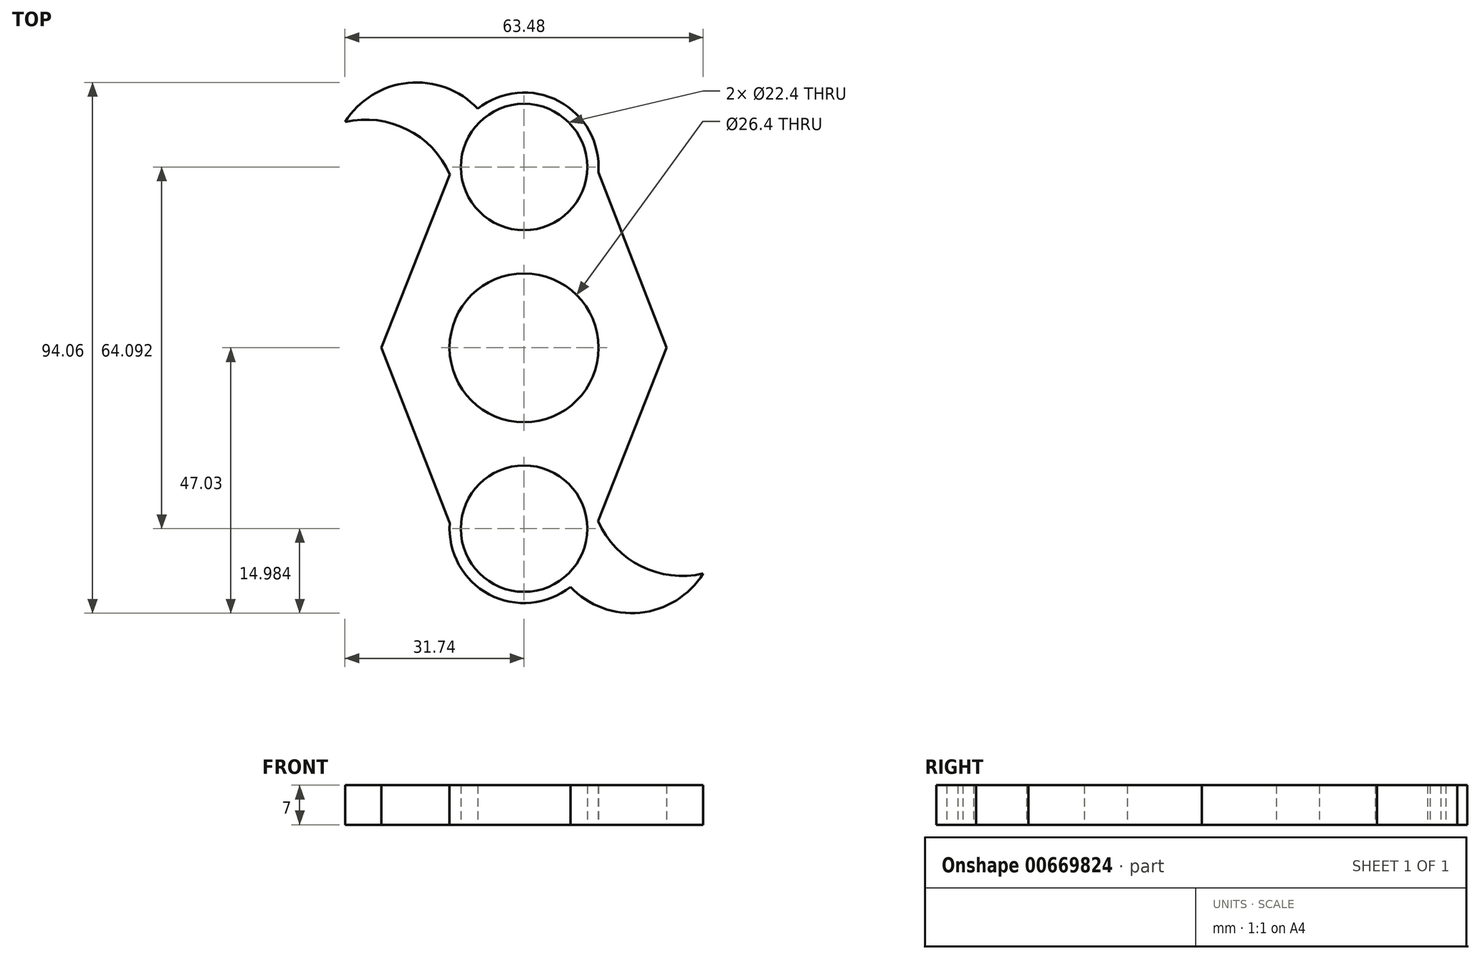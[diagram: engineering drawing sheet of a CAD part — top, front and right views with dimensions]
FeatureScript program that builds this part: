
annotation { "Feature Type Name" : "Feature", "Feature Type Description" : "" }
export const myFeature = defineFeature(function(context is Context, id is Id, definition is map)
    precondition{}
    {
        {
            var Q0;
            Q0=qCreatedBy(makeId("Top.planeOp"),FACE);
            var sketch = newSketch(context, id + "F0", { "sketchPlane" : qUnion([Q0])});
            skCircle(sketch, "E0", {"center": v(0, 0) * mm, "radius": 11.2 * mm});
            skCircle(sketch, "E1", {"center": v(0, 0) * mm, "radius": 13.2 * mm});
            skCircle(sketch, "E2", {"center": v(0, 32.05) * mm, "radius": 11.2 * mm});
            skCircle(sketch, "E3", {"center": v(0, 32.05) * mm, "radius": 13.2 * mm});
            skCircle(sketch, "E4.1.0", {"center": v(0, -32.05) * mm, "radius": 13.2 * mm});
            skCircle(sketch, "E4.1.1", {"center": v(0, -32.05) * mm, "radius": 11.2 * mm});
            skLineSegment(sketch, "E5", {"start": v(-13.13, 30.73) * mm, "end": v(-25.26, 0) * mm});
            skLineSegment(sketch, "E6", {"start": v(-25.26, 0) * mm, "end": v(-13.16, -31.07) * mm});
            skLineSegment(sketch, "E7.1.0", {"start": v(13.13, -30.73) * mm, "end": v(25.26, 0) * mm});
            skLineSegment(sketch, "E7.1.1", {"start": v(25.26, 0) * mm, "end": v(13.16, 31.07) * mm});
            skArc(sketch, "E8", {"start": v(-13.13, 30.73) * mm, "mid": v(-20.76, 38.72) * mm, "end": v(-31.74, 40) * mm});
            skArc(sketch, "E9", {"start": v(-8.22, 42.38) * mm, "mid": v(-20.56, 46.95) * mm, "end": v(-31.74, 40) * mm});
            skArc(sketch, "E10.1.0", {"start": v(8.22, -42.38) * mm, "mid": v(20.56, -46.95) * mm, "end": v(31.74, -40) * mm});
            skArc(sketch, "E10.1.1", {"start": v(13.13, -30.73) * mm, "mid": v(20.76, -38.72) * mm, "end": v(31.74, -40) * mm});
            skSolve(sketch);
        }
        {
            var Q0;
            Q0=makeQuery(id+"F0.imprint","IMPRINT",FACE,{"disambiguationData":[TD([[makeQuery(id+"F0.imprint","IMPRINT",EDGE,{"derivedFrom":sQuery(id+"F0.wireOp",EDGE,"E1")}),-1.0]])]});
            var Q1;
            Q1=makeQuery(id+"F0.imprint","IMPRINT",FACE,{"disambiguationData":[TD([[makeQuery(id+"F0.imprint","IMPRINT",EDGE,{"derivedFrom":sQuery(id+"F0.wireOp",EDGE,"E2")}),-1.0]])]});
            var Q2;
            {var subQ0=sQuery(id+"F0.wireOp",EDGE,"E8");Q2=makeQuery(id+"F0.imprint","IMPRINT",FACE,{"disambiguationData":[TD([[makeQuery(id+"F0.imprint","IMPRINT",EDGE,{"derivedFrom":subQ0}),-1.0]])]});}
            var Q3;
            Q3=makeQuery(id+"F0.imprint","IMPRINT",FACE,{"disambiguationData":[TD([[makeQuery(id+"F0.imprint","IMPRINT",EDGE,{"derivedFrom":sQuery(id+"F0.wireOp",EDGE,"E4.1.1")}),-1.0]])]});
            var Q4;
            {var subQ2=sQuery(id+"F0.wireOp",EDGE,"E10.1.0");Q4=makeQuery(id+"F0.imprint","IMPRINT",FACE,{"disambiguationData":[TD([[makeQuery(id+"F0.imprint","IMPRINT",EDGE,{"derivedFrom":subQ2}),1.0]])]});}
            extrude(context, id + "F1", {"entities" : qUnion([Q0, Q1, Q2, Q3, Q4]), "depth" : 7 * mm, "offsetDistance" : 25 * mm});
        }
    });
